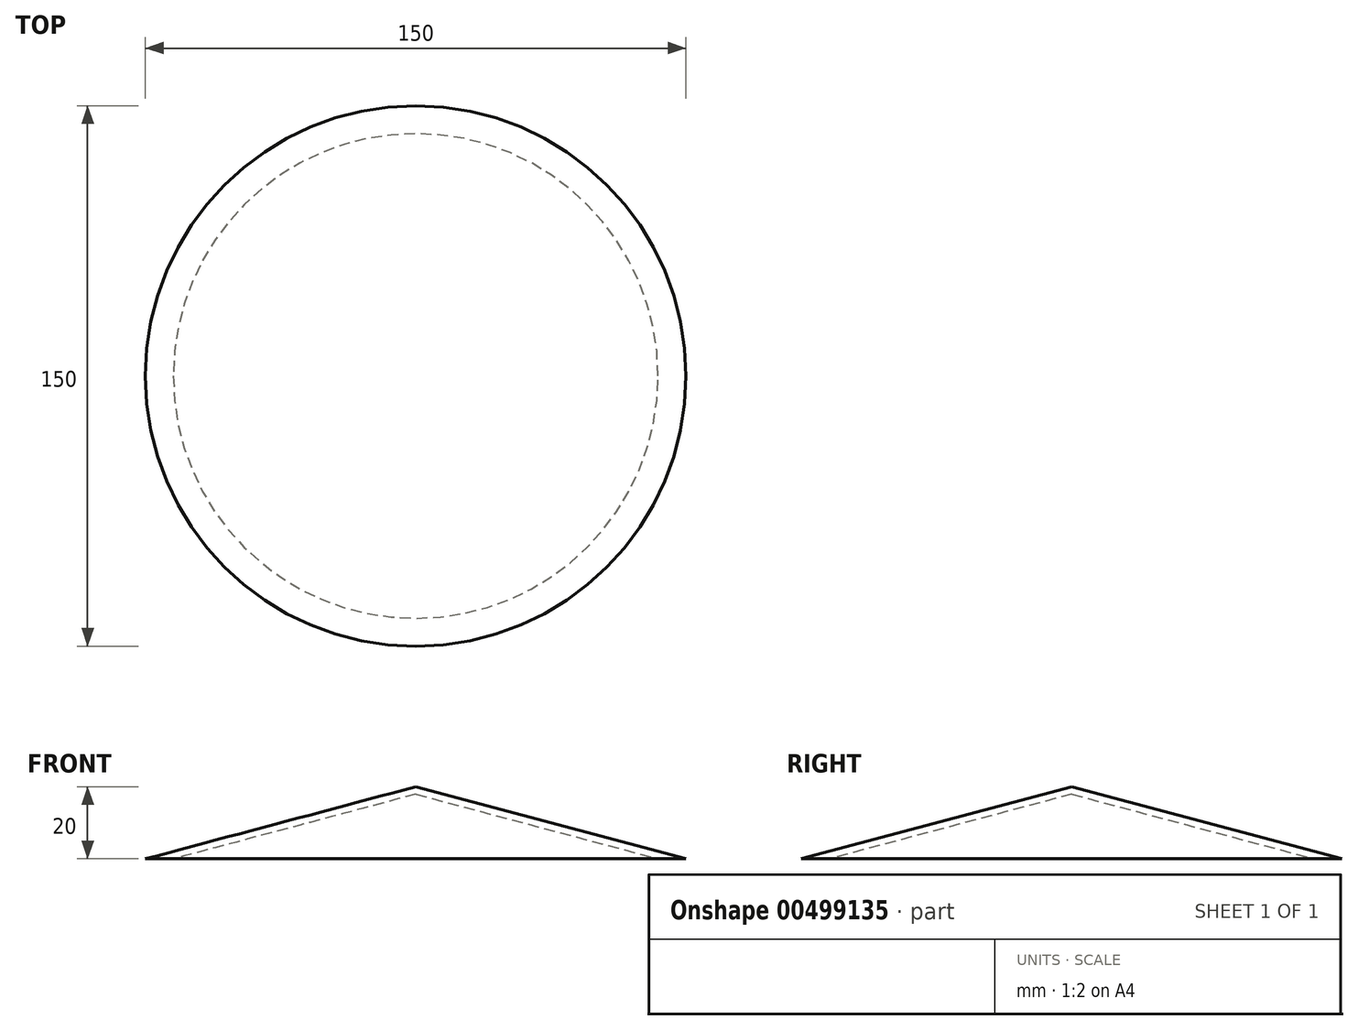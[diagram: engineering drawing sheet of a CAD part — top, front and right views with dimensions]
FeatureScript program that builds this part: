
annotation { "Feature Type Name" : "Feature", "Feature Type Description" : "" }
export const myFeature = defineFeature(function(context is Context, id is Id, definition is map)
    precondition{}
    {
        {
            var Q0;
            Q0=qCreatedBy(makeId("Top.planeOp"),FACE);
            cPlane(context, id + "F0", {"entities" : qUnion([Q0]), "cplaneType" : CPlaneType.OFFSET, "offset" : 20 * mm, "oppositeDirection" : true, "width" : 150 * mm, "height" : 150 * mm});
        }
        {
            var Q0;
            Q0=qCreatedBy(id+"F0.planeOp",FACE);
            var sketch = newSketch(context, id + "F1", { "sketchPlane" : qUnion([Q0])});
            skCircle(sketch, "E0", {"center": v(0, 0) * mm, "radius": 75 * mm});
            skSolve(sketch);
        }
        {
            var Q0;
            Q0=makeQuery(id+"F1.imprint","IMPRINT",FACE,{"disambiguationData":[TD([[makeQuery(id+"F1.imprint","IMPRINT",EDGE,{"derivedFrom":sQuery(id+"F1.wireOp",EDGE,"E0")}),1.0]])]});
            var Q1;
            Q1=qCreatedBy(makeId("Origin.pointOp"),VERTEX);
            loft(context, id + "F2", {"sheetProfilesArray" : [{ "sheetProfileEntities" : qUnion([Q0]) }, { "sheetProfileEntities" : qUnion([Q1]) }]});
        }
        {
            var Q0;
            Q0=makeQuery(id+"F2.opLoft","CAP_FACE",FACE,{"disambiguationData":[OSD([makeQuery(id+"F1.imprint","IMPRINT",FACE,{"disambiguationData":[TD([[makeQuery(id+"F1.imprint","IMPRINT",EDGE,{"derivedFrom":sQuery(id+"F1.wireOp",EDGE,"E0")}),1.0]])]})])],"isStart":true});
            shell(context, id + "F3", {"entities" : qUnion([Q0]), "thickness" : 2 * mm});
        }
    });
